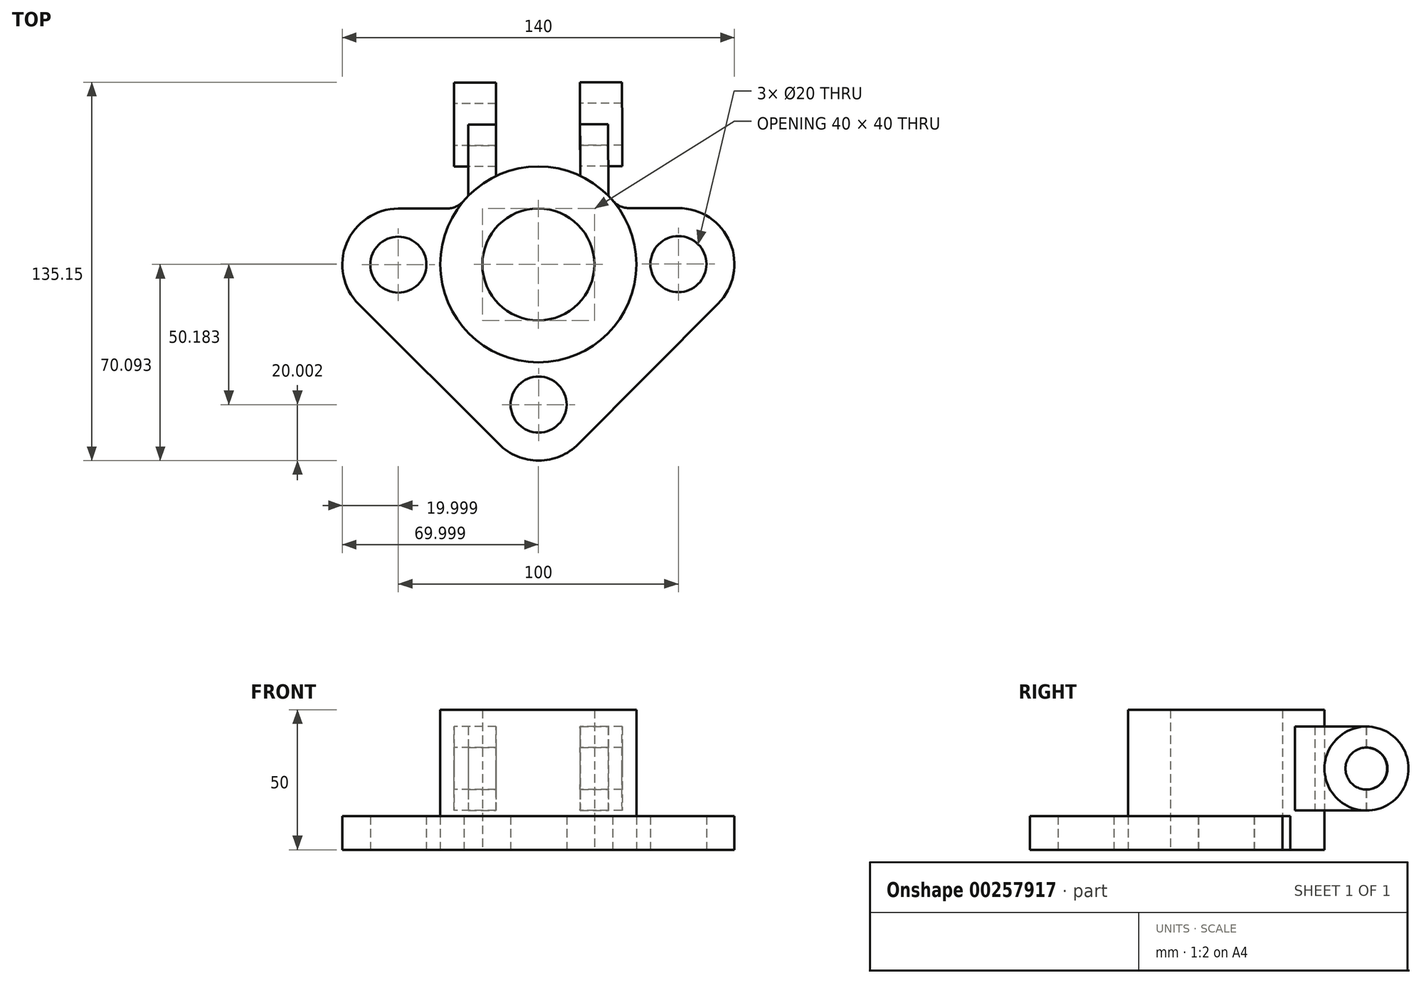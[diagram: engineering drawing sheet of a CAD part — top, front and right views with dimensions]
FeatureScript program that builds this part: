
annotation { "Feature Type Name" : "Feature", "Feature Type Description" : "" }
export const myFeature = defineFeature(function(context is Context, id is Id, definition is map)
    precondition{}
    {
        {
            var Q0;
            Q0=qCreatedBy(makeId("Top.planeOp"),FACE);
            var sketch = newSketch(context, id + "F0", { "sketchPlane" : qUnion([Q0])});
            skArc(sketch, "E0", {"start": v(-50.04, 20.44) * mm, "mid": v(-68.52, 8.09) * mm, "end": v(-64.17, -13.71) * mm});
            skCircle(sketch, "E1", {"center": v(-50.04, 0.44) * mm, "radius": 10 * mm});
            skLineSegment(sketch, "E2", {"start": v(0, -40.88) * mm, "end": v(0, -72.38) * mm, "construction": true});
            skArc(sketch, "E3", {"start": v(-14.08, -63.71) * mm, "mid": v(0.09, -69.56) * mm, "end": v(14.23, -63.66) * mm});
            skLineSegment(sketch, "E4", {"start": v(-64.17, -13.71) * mm, "end": v(-14.08, -63.71) * mm});
            skCircle(sketch, "E5", {"center": v(0.05, -49.56) * mm, "radius": 10 * mm});
            skLineSegment(sketch, "E6", {"start": v(0.05, -49.56) * mm, "end": v(0, -21.91) * mm, "construction": true});
            skArc(sketch, "E7.MirrorC", {"start": v(49.92, 20.62) * mm, "mid": v(68.42, 8.32) * mm, "end": v(64.14, -13.48) * mm});
            skCircle(sketch, "E8.MirrorC", {"center": v(49.96, 0.62) * mm, "radius": 10 * mm});
            skLineSegment(sketch, "E9.MirrorCS", {"start": v(64.14, -13.48) * mm, "end": v(14.23, -63.66) * mm});
            skLineSegment(sketch, "E10", {"start": v(-50.04, 0.44) * mm, "end": v(-50.04, 28.13) * mm, "construction": true});
            skLineSegment(sketch, "E11", {"start": v(49.96, 0.62) * mm, "end": v(49.96, 25.22) * mm, "construction": true});
            skPoint(sketch, "E12.newPointA", {"position": v(22, 23.57) * mm});
            skPoint(sketch, "E12.newPointB", {"position": v(-50.04, 20.44) * mm});
            skPoint(sketch, "E13.orphan", {"position": v(-30.16, 20.48) * mm});
            skLineSegment(sketch, "E14", {"start": v(-50.04, 0.44) * mm, "end": v(49.96, 0.62) * mm, "construction": true});
            skLineSegment(sketch, "E15", {"start": v(0, -21.91) * mm, "end": v(-0.2, 84.2) * mm, "construction": true});
            skCircle(sketch, "E16", {"center": v(-0.04, 0.53) * mm, "radius": 35 * mm});
            skCircle(sketch, "E17", {"center": v(-0.04, 0.53) * mm, "radius": 20 * mm});
            skLineSegment(sketch, "E18", {"start": v(-50.04, 20.44) * mm, "end": v(-32.71, 20.47) * mm});
            skArc(sketch, "E19", {"start": v(-32.71, 20.47) * mm, "mid": v(-29.37, 21.21) * mm, "end": v(-26.65, 23.28) * mm});
            skLineSegment(sketch, "E20.trimOffspring", {"start": v(-0.1, 20.53) * mm, "end": v(-0.05, 20.53) * mm});
            skLineSegment(sketch, "E21", {"start": v(49.92, 20.62) * mm, "end": v(32.56, 20.6) * mm});
            skArc(sketch, "E22", {"start": v(26.48, 23.37) * mm, "mid": v(29.21, 21.32) * mm, "end": v(32.56, 20.6) * mm});
            skLineSegment(sketch, "E23", {"start": v(49.96, 0.62) * mm, "end": v(49.87, 50.62) * mm, "construction": true});
            skLineSegment(sketch, "E24", {"start": v(49.87, 50.62) * mm, "end": v(29.87, 50.59) * mm, "construction": true});
            skLineSegment(sketch, "E25", {"start": v(14.87, 50.56) * mm, "end": v(14.9, 32.18) * mm});
            skLineSegment(sketch, "E26", {"start": v(14.87, 50.56) * mm, "end": v(24.87, 50.58) * mm});
            skLineSegment(sketch, "E27", {"start": v(24.87, 50.58) * mm, "end": v(24.91, 25.07) * mm});
            skLineSegment(sketch, "E28.trimOffspring", {"start": v(-0.13, 50.53) * mm, "end": v(-10.19, 50.51) * mm, "construction": true});
            skLineSegment(sketch, "E29.MirrorCS", {"start": v(-15.13, 50.5) * mm, "end": v(-15.1, 32.13) * mm});
            skLineSegment(sketch, "E30.MirrorCS", {"start": v(-15.13, 50.5) * mm, "end": v(-25.13, 50.49) * mm});
            skLineSegment(sketch, "E31.MirrorCS", {"start": v(-25.13, 50.49) * mm, "end": v(-25.09, 24.98) * mm});
            skSolve(sketch);
        }
        {
            var Q0;
            Q0=makeQuery(id+"F0.imprint","IMPRINT",FACE,{"disambiguationData":[TD([[makeQuery(id+"F0.imprint","IMPRINT",EDGE,{"derivedFrom":sQuery(id+"F0.wireOp",EDGE,"E1")}),-1.0]])]});
            extrude(context, id + "F1", {"entities" : qUnion([Q0]), "depth" : 12 * mm});
        }
        {
            var Q0;
            {var subQ3=sQuery(id+"F0.wireOp",EDGE,"E17");var subQ4=makeQuery(id+"F0.imprint","IMPRINT",VERTEX,{"disambiguationData":[OD(0.0)],"derivedFrom":subQ3});Q0=makeQuery(id+"F0.imprint","IMPRINT",FACE,{"disambiguationData":[TD([[makeQuery(id+"F0.imprint","IMPRINT",EDGE,{"disambiguationData":[TD([[subQ4,1.0]])],"derivedFrom":subQ3}),-1.0]])]});}
            extrude(context, id + "F2", {"entities" : qUnion([Q0]), "depth" : 50 * mm});
        }
        {
            var Q0;
            {var subQ0=sQuery(id+"F0.wireOp",EDGE,"E25");Q0=makeQuery(id+"F0.imprint","IMPRINT",FACE,{"disambiguationData":[TD([[makeQuery(id+"F0.imprint","IMPRINT",EDGE,{"derivedFrom":subQ0}),1.0]])]});}
            var Q1;
            {var subQ0=sQuery(id+"F0.wireOp",EDGE,"E29.MirrorCS");Q1=makeQuery(id+"F0.imprint","IMPRINT",FACE,{"disambiguationData":[TD([[makeQuery(id+"F0.imprint","IMPRINT",EDGE,{"derivedFrom":subQ0}),-1.0]])]});}
            extrude(context, id + "F3", {"entities" : qUnion([Q0, Q1]), "depth" : 44 * mm});
        }
        {
            var Q0;
            Q0=makeQuery(id+"F3.opExtrude","SWEPT_FACE",FACE,{"disambiguationData":[OSD([sQuery(id+"F0.wireOp",EDGE,"E27")])]});
            var sketch = newSketch(context, id + "F4", { "sketchPlane" : qUnion([Q0])});
            skLineSegment(sketch, "E32", {"start": v(50.53, 0) * mm, "end": v(50.53, 14) * mm});
            skLineSegment(sketch, "E33", {"start": v(50.53, 14) * mm, "end": v(25.03, 14) * mm});
            skLineSegment(sketch, "E34", {"start": v(25.03, 14) * mm, "end": v(25.03, 0) * mm});
            skLineSegment(sketch, "E35", {"start": v(25.03, 0) * mm, "end": v(50.53, 0) * mm});
            skSolve(sketch);
        }
        {
            var Q0;
            Q0=makeQuery(id+"F4.imprint","IMPRINT",FACE,{"disambiguationData":[TD([[makeQuery(id+"F4.imprint","IMPRINT",EDGE,{"derivedFrom":sQuery(id+"F4.wireOp",EDGE,"E32")}),-1.0]])]});
            extrude(context, id + "F5", {"entities" : qUnion([Q0]), "oppositeDirection" : true, "depth" : 100 * mm});
        }
        {
            var Q0;
            Q0=makeQuery(id+"F5.opExtrude","SWEPT_BODY",BODY,{"disambiguationData":[OSD([sQuery(id+"F4.wireOp",EDGE,"E32"),sQuery(id+"F4.wireOp",EDGE,"E33"),sQuery(id+"F4.wireOp",EDGE,"E34"),sQuery(id+"F4.wireOp",EDGE,"E35")])]});
            var Q1;
            Q1=makeQuery(id+"F3.opExtrude","SWEPT_BODY",BODY,{"disambiguationData":[OSD([sQuery(id+"F0.wireOp",EDGE,"E16"),sQuery(id+"F0.wireOp",EDGE,"E25"),sQuery(id+"F0.wireOp",EDGE,"E26"),sQuery(id+"F0.wireOp",EDGE,"E27")])]});
            var Q2;
            Q2=makeQuery(id+"F3.opExtrude","SWEPT_BODY",BODY,{"disambiguationData":[OSD([sQuery(id+"F0.wireOp",EDGE,"E16"),sQuery(id+"F0.wireOp",EDGE,"E29.MirrorCS"),sQuery(id+"F0.wireOp",EDGE,"E30.MirrorCS"),sQuery(id+"F0.wireOp",EDGE,"E31.MirrorCS")])]});
            booleanBodies(context, id + "F6", {"operationType" : BooleanOperationType.SUBTRACTION, "tools" : qUnion([Q0]), "targets" : qUnion([Q1, Q2])});
        }
        {
            var Q0;
            Q0=makeQuery(id+"F3.opExtrude","SWEPT_FACE",FACE,{"disambiguationData":[OSD([sQuery(id+"F0.wireOp",EDGE,"E27")])]});
            var sketch = newSketch(context, id + "F7", { "sketchPlane" : qUnion([Q0])});
            skCircle(sketch, "E36", {"center": v(50.53, 29) * mm, "radius": 15 * mm});
            skCircle(sketch, "E37", {"center": v(50.53, 29) * mm, "radius": 7.5 * mm});
            skSolve(sketch);
        }
        {
            var Q0;
            {var subQ1=sQuery(id+"F0.wireOp",EDGE,"E27");var subQ2=makeQuery(id+"F3.opExtrude","SWEPT_EDGE",EDGE,{"disambiguationData":[OSD([sQuery(id+"F0.wireOp",EDGE,"E26"),subQ1])]});var subQ5=sQuery(id+"F7.wireOp",EDGE,"E37");var subQ6=makeQuery(id+"F7.imprint","INTERSECT",VERTEX,{"disambiguationData":[OD(0.0)],"derivedFrom":[subQ2,subQ5]});Q0=makeQuery(id+"F7.imprint","IMPRINT",FACE,{"disambiguationData":[TD([[makeQuery(id+"F7.imprint","IMPRINT",EDGE,{"disambiguationData":[TD([[subQ6,1.0]])],"derivedFrom":subQ5}),-1.0]])]});}
            var Q1;
            {var subQ1=sQuery(id+"F0.wireOp",EDGE,"E27");var subQ2=makeQuery(id+"F3.opExtrude","SWEPT_EDGE",EDGE,{"disambiguationData":[OSD([sQuery(id+"F0.wireOp",EDGE,"E26"),subQ1])]});var subQ5=sQuery(id+"F7.wireOp",EDGE,"E37");var subQ6=makeQuery(id+"F7.imprint","INTERSECT",VERTEX,{"disambiguationData":[OD(0.0)],"derivedFrom":[subQ2,subQ5]});Q1=makeQuery(id+"F7.imprint","IMPRINT",FACE,{"disambiguationData":[TD([[makeQuery(id+"F7.imprint","IMPRINT",EDGE,{"disambiguationData":[TD([[subQ6,-1.0]])],"derivedFrom":subQ5}),-1.0]])]});}
            extrude(context, id + "F8", {"entities" : qUnion([Q0, Q1]), "depth" : 5 * mm, "hasSecondDirection" : true, "secondDirectionOppositeDirection" : true, "secondDirectionDepth" : 55 * mm});
        }
        {
            var Q0;
            {var subQ0=sQuery(id+"F7.wireOp",EDGE,"E37");var subQ1=makeQuery(id+"F3.opExtrude","SWEPT_EDGE",EDGE,{"disambiguationData":[OSD([sQuery(id+"F0.wireOp",EDGE,"E26"),sQuery(id+"F0.wireOp",EDGE,"E27")])]});var subQ2=makeQuery(id+"F7.imprint","INTERSECT",VERTEX,{"disambiguationData":[OD(0.0)],"derivedFrom":[subQ1,subQ0]});Q0=makeQuery(id+"F7.imprint","IMPRINT",FACE,{"disambiguationData":[TD([[makeQuery(id+"F7.imprint","IMPRINT",EDGE,{"disambiguationData":[TD([[subQ2,1.0]])],"derivedFrom":subQ0}),1.0]])]});}
            var Q1;
            {var subQ0=sQuery(id+"F7.wireOp",EDGE,"E37");var subQ1=makeQuery(id+"F3.opExtrude","SWEPT_EDGE",EDGE,{"disambiguationData":[OSD([sQuery(id+"F0.wireOp",EDGE,"E26"),sQuery(id+"F0.wireOp",EDGE,"E27")])]});var subQ2=makeQuery(id+"F7.imprint","INTERSECT",VERTEX,{"disambiguationData":[OD(0.0)],"derivedFrom":[subQ1,subQ0]});Q1=makeQuery(id+"F7.imprint","IMPRINT",FACE,{"disambiguationData":[TD([[makeQuery(id+"F7.imprint","IMPRINT",EDGE,{"disambiguationData":[TD([[subQ2,-1.0]])],"derivedFrom":subQ0}),1.0]])]});}
            extrude(context, id + "F9", {"entities" : qUnion([Q0, Q1]), "oppositeDirection" : true, "depth" : 100 * mm, "hasSecondDirection" : true, "secondDirectionOppositeDirection" : false, "secondDirectionDepth" : 25 * mm});
        }
        {
            var Q0;
            Q0=makeQuery(id+"F9.opExtrude","SWEPT_BODY",BODY,{"disambiguationData":[OSD([sQuery(id+"F7.wireOp",EDGE,"E37")])]});
            var Q1;
            Q1=makeQuery(id+"F3.opExtrude","SWEPT_BODY",BODY,{"disambiguationData":[OSD([sQuery(id+"F0.wireOp",EDGE,"E16"),sQuery(id+"F0.wireOp",EDGE,"E25"),sQuery(id+"F0.wireOp",EDGE,"E26"),sQuery(id+"F0.wireOp",EDGE,"E27")])]});
            var Q2;
            Q2=makeQuery(id+"F3.opExtrude","SWEPT_BODY",BODY,{"disambiguationData":[OSD([sQuery(id+"F0.wireOp",EDGE,"E16"),sQuery(id+"F0.wireOp",EDGE,"E29.MirrorCS"),sQuery(id+"F0.wireOp",EDGE,"E30.MirrorCS"),sQuery(id+"F0.wireOp",EDGE,"E31.MirrorCS")])]});
            booleanBodies(context, id + "F10", {"operationType" : BooleanOperationType.SUBTRACTION, "tools" : qUnion([Q0]), "targets" : qUnion([Q1, Q2])});
        }
        {
            var Q0;
            Q0=makeQuery(id+"F3.opExtrude","CAP_FACE",FACE,{"disambiguationData":[OSD([sQuery(id+"F0.wireOp",EDGE,"E16"),sQuery(id+"F0.wireOp",EDGE,"E25"),sQuery(id+"F0.wireOp",EDGE,"E26"),sQuery(id+"F0.wireOp",EDGE,"E27")])],"isStart":false});
            var sketch = newSketch(context, id + "F11", { "sketchPlane" : qUnion([Q0])});
            skPoint(sketch, "E38.endSnap0", {"position": v(19.87, 50.57) * mm});
            skLineSegment(sketch, "E39", {"start": v(14.87, 50.56) * mm, "end": v(14.83, 69.27) * mm});
            skLineSegment(sketch, "E40", {"start": v(14.83, 69.27) * mm, "end": v(-15.13, 69.21) * mm});
            skLineSegment(sketch, "E41", {"start": v(-15.13, 69.21) * mm, "end": v(-15.13, 50.57) * mm});
            skLineSegment(sketch, "E42", {"start": v(14.87, 50.56) * mm, "end": v(14.9, 28.06) * mm});
            skLineSegment(sketch, "E43", {"start": v(14.9, 28.06) * mm, "end": v(-15.13, 28) * mm});
            skLineSegment(sketch, "E44", {"start": v(-15.13, 28) * mm, "end": v(-15.13, 50.57) * mm});
            skSolve(sketch);
        }
        {
            var Q0;
            {var subQ1=sQuery(id+"F11.wireOp",EDGE,"E39");Q0=makeQuery(id+"F11.imprint","IMPRINT",FACE,{"disambiguationData":[TD([[makeQuery(id+"F11.imprint","IMPRINT",EDGE,{"derivedFrom":subQ1}),1.0]])]});}
            extrude(context, id + "F12", {"entities" : qUnion([Q0]), "oppositeDirection" : true, "depth" : 50 * mm});
        }
        {
            var Q0;
            Q0=makeQuery(id+"F12.opExtrude","SWEPT_BODY",BODY,{"disambiguationData":[OSD([sQuery(id+"F11.wireOp",EDGE,"E39"),sQuery(id+"F11.wireOp",EDGE,"E40"),sQuery(id+"F11.wireOp",EDGE,"E41"),sQuery(id+"F11.wireOp",EDGE,"E42"),sQuery(id+"F11.wireOp",EDGE,"E43"),sQuery(id+"F11.wireOp",EDGE,"E44")])]});
            var Q1;
            Q1=makeQuery(id+"F8.opExtrude","SWEPT_BODY",BODY,{"disambiguationData":[OSD([sQuery(id+"F7.wireOp",EDGE,"E36"),sQuery(id+"F7.wireOp",EDGE,"E37")])]});
            booleanBodies(context, id + "F13", {"operationType" : BooleanOperationType.SUBTRACTION, "tools" : qUnion([Q0]), "targets" : qUnion([Q1])});
        }
    });
